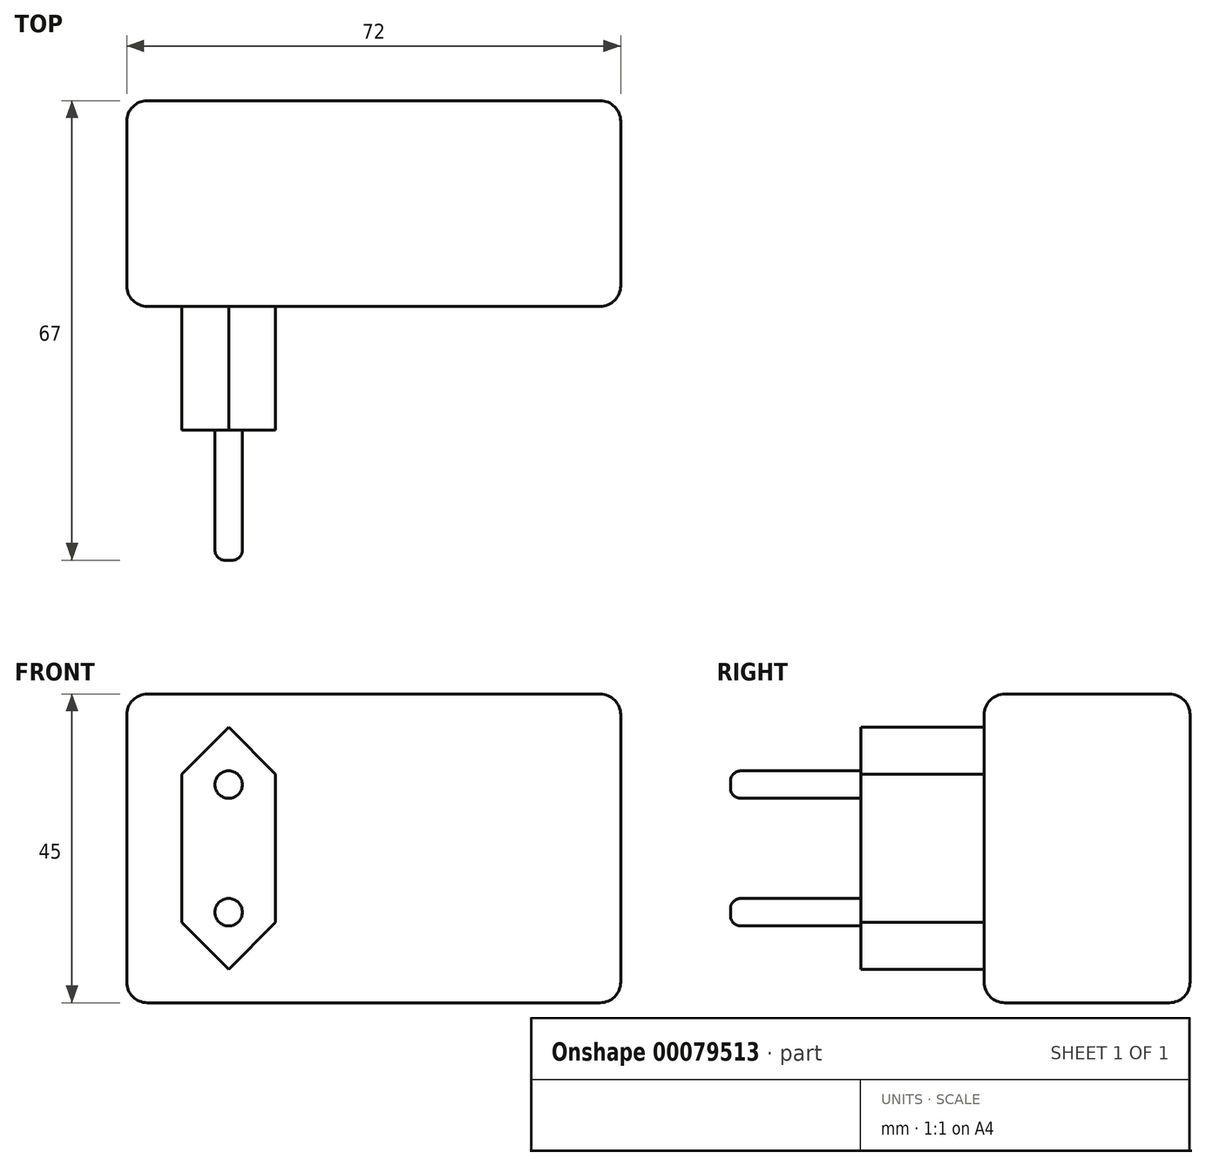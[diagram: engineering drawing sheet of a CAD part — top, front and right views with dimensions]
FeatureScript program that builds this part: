
annotation { "Feature Type Name" : "Feature", "Feature Type Description" : "" }
export const myFeature = defineFeature(function(context is Context, id is Id, definition is map)
    precondition{}
    {
        {
            var Q0;
            Q0=qCreatedBy(makeId("Front.planeOp"),FACE);
            var sketch = newSketch(context, id + "F0", { "sketchPlane" : qUnion([Q0])});
            skLineSegment(sketch, "E0.bottom", {"start": v(-72, 22.5) * mm, "end": v(0, 22.5) * mm});
            skLineSegment(sketch, "E0.top", {"start": v(-72, -22.5) * mm, "end": v(0, -22.5) * mm});
            skLineSegment(sketch, "E0.left", {"start": v(-72, 22.5) * mm, "end": v(-72, -22.5) * mm});
            skLineSegment(sketch, "E0.right", {"start": v(0, 22.5) * mm, "end": v(0, -22.5) * mm});
            skSolve(sketch);
        }
        {
            var Q0;
            Q0 = qSketchRegion(id + "F0", true);
            extrude(context, id + "F1", {"entities" : qUnion([Q0]), "oppositeDirection" : true, "depth" : 30 * mm});
        }
        {
            var Q0;
            Q0=makeQuery(id+"F1.opExtrude","CAP_FACE",FACE,{"disambiguationData":[OSD([sQuery(id+"F0.wireOp",EDGE,"E0.bottom"),sQuery(id+"F0.wireOp",EDGE,"E0.top"),sQuery(id+"F0.wireOp",EDGE,"E0.left"),sQuery(id+"F0.wireOp",EDGE,"E0.right")])],"isStart":true});
            var sketch = newSketch(context, id + "F2", { "sketchPlane" : qUnion([Q0])});
            skLineSegment(sketch, "E1", {"start": v(-64, -10.8) * mm, "end": v(-64, 10.8) * mm});
            skLineSegment(sketch, "E2", {"start": v(-64, 10.8) * mm, "end": v(-57.15, 17.65) * mm});
            skLineSegment(sketch, "E3", {"start": v(-57.15, 17.65) * mm, "end": v(-50.3, 10.8) * mm});
            skLineSegment(sketch, "E4", {"start": v(-50.3, 10.8) * mm, "end": v(-50.3, -10.8) * mm});
            skLineSegment(sketch, "E5", {"start": v(-50.3, -10.8) * mm, "end": v(-57.15, -17.65) * mm});
            skLineSegment(sketch, "E6", {"start": v(-57.15, -17.65) * mm, "end": v(-64, -10.8) * mm});
            skSolve(sketch);
        }
        {
            var Q0;
            Q0=makeQuery(id+"F2.imprint","IMPRINT",FACE,{"disambiguationData":[TD([[makeQuery(id+"F2.imprint","IMPRINT",EDGE,{"derivedFrom":sQuery(id+"F2.wireOp",EDGE,"E1")}),-1.0]])]});
            extrude(context, id + "F3", {"entities" : qUnion([Q0]), "operationType" : NewBodyOperationType.ADD, "depth" : 18 * mm});
        }
        {
            var Q0;
            Q0=makeQuery(id+"F3.opExtrude","CAP_FACE",FACE,{"disambiguationData":[OSD([sQuery(id+"F2.wireOp",EDGE,"E1"),sQuery(id+"F2.wireOp",EDGE,"E2"),sQuery(id+"F2.wireOp",EDGE,"E3"),sQuery(id+"F2.wireOp",EDGE,"E4"),sQuery(id+"F2.wireOp",EDGE,"E5"),sQuery(id+"F2.wireOp",EDGE,"E6")])],"isStart":false});
            var sketch = newSketch(context, id + "F4", { "sketchPlane" : qUnion([Q0])});
            skLineSegment(sketch, "E7", {"start": v(-57.15, 17.65) * mm, "end": v(-57.15, -17.65) * mm, "construction": true});
            skCircle(sketch, "E8", {"center": v(-57.15, 9.3) * mm, "radius": 2 * mm});
            skCircle(sketch, "E9", {"center": v(-57.15, -9.3) * mm, "radius": 2 * mm});
            skSolve(sketch);
        }
        {
            var Q0;
            Q0 = qSketchRegion(id + "F4", true);
            extrude(context, id + "F5", {"entities" : qUnion([Q0]), "operationType" : NewBodyOperationType.ADD, "depth" : 19 * mm});
        }
        {
            var Q0;
            Q0=makeQuery(id+"F5.opExtrude","CAP_EDGE",EDGE,{"disambiguationData":[OSD([sQuery(id+"F4.wireOp",EDGE,"E8")])],"isStart":false});
            var Q1;
            Q1=makeQuery(id+"F5.opExtrude","CAP_EDGE",EDGE,{"disambiguationData":[OSD([sQuery(id+"F4.wireOp",EDGE,"E9")])],"isStart":false});
            fillet(context, id + "F6", {"entities" : qUnion([Q0, Q1]), "radius" : 1.5 * mm, "tangentPropagation" : true, "allowEdgeOverflow" : false});
        }
        {
            var Q0;
            Q0=makeQuery(id+"F1.opExtrude","SWEPT_FACE",FACE,{"disambiguationData":[OSD([sQuery(id+"F0.wireOp",EDGE,"E0.left")])]});
            var Q1;
            Q1=makeQuery(id+"F1.opExtrude","SWEPT_FACE",FACE,{"disambiguationData":[OSD([sQuery(id+"F0.wireOp",EDGE,"E0.right")])]});
            var Q2;
            Q2=makeQuery(id+"F1.opExtrude","SWEPT_FACE",FACE,{"disambiguationData":[OSD([sQuery(id+"F0.wireOp",EDGE,"E0.bottom")])]});
            var Q3;
            Q3=makeQuery(id+"F1.opExtrude","SWEPT_FACE",FACE,{"disambiguationData":[OSD([sQuery(id+"F0.wireOp",EDGE,"E0.top")])]});
            fillet(context, id + "F7", {"entities" : qUnion([Q0, Q1, Q2, Q3]), "radius" : 3 * mm, "tangentPropagation" : true, "allowEdgeOverflow" : false});
        }
    });
